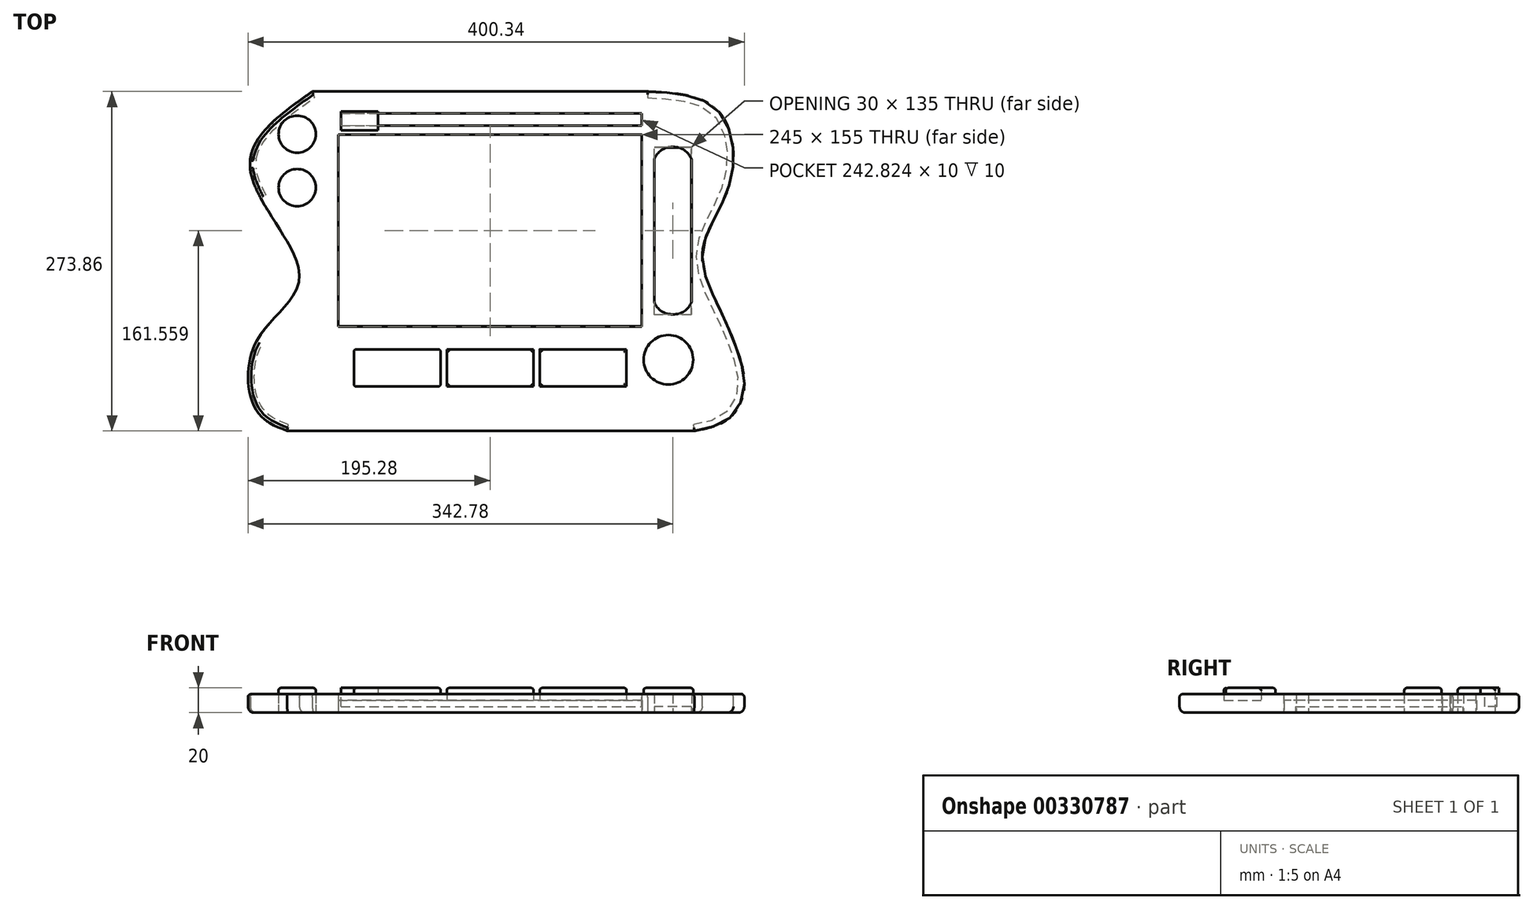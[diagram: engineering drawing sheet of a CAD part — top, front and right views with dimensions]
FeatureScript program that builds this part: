
annotation { "Feature Type Name" : "Feature", "Feature Type Description" : "" }
export const myFeature = defineFeature(function(context is Context, id is Id, definition is map)
    precondition{}
    {
        {
            var Q0;
            Q0=qCreatedBy(makeId("Top.planeOp"),FACE);
            var sketch = newSketch(context, id + "F0", { "sketchPlane" : qUnion([Q0])});
            skLineSegment(sketch, "E0.bottom", {"start": v(164.72, -136.93) * mm, "end": v(-163.68, -136.93) * mm});
            skLineSegment(sketch, "E0.top", {"start": v(127.2, 136.93) * mm, "end": v(-143.35, 136.93) * mm});
            skPoint(sketch, "E0.middle", {"position": v(0, 0) * mm});
            skFitSpline(sketch, "E1", {"points": [v(-143.35, 136.93) * mm, v(-193.66, 75.02) * mm, v(-153.78, -11.5) * mm, v(-188.18, -64.16) * mm, v(-188.7, -119.93) * mm, v(-163.68, -136.93) * mm], "startDerivative": vector(-350.4, -246.16) * mm, "endDerivative": vector(205.8, -79.15) * mm});
            skPoint(sketch, "E2.orphan", {"position": v(-193.66, 136.93) * mm});
            skLineSegment(sketch, "E3.trimOffspring", {"start": v(-193.66, 75.02) * mm, "end": v(-193.66, 81.28) * mm});
            skPoint(sketch, "E4.orphan", {"position": v(-193.66, -136.93) * mm});
            skFitSpline(sketch, "E5", {"points": [v(127.2, 136.93) * mm, v(183.49, 121.94) * mm, v(193.66, 64.08) * mm, v(171.5, 9.34) * mm, v(186.1, -40.7) * mm, v(204.86, -94.4) * mm, v(199.65, -118.9) * mm, v(186.62, -130.88) * mm, v(164.72, -136.93) * mm], "startDerivative": vector(444.92, -23.16) * mm, "endDerivative": vector(-254.64, -48.14) * mm});
            skPoint(sketch, "E6.orphan", {"position": v(193.66, 136.93) * mm});
            skPoint(sketch, "E0.left.start.orphan", {"position": v(193.66, -136.93) * mm});
            skFitSpline(sketch, "E7", {"points": [v(-193.66, 81.28) * mm, v(-184.53, 113.6) * mm, v(-160.55, 132.36) * mm, v(-143.35, 136.93) * mm], "startDerivative": vector(12.3, 93.1) * mm, "endDerivative": vector(59.92, 10.35) * mm});
            skFitSpline(sketch, "E8", {"points": [v(-184.98, 50.85) * mm, v(-169.94, 0) * mm, v(-176.2, -30.8) * mm, v(-188.18, -64.16) * mm], "startDerivative": vector(55.2, -140.26) * mm, "endDerivative": vector(-39.02, -107.81) * mm});
            skLineSegment(sketch, "E9.bottom", {"start": v(122.5, 102.13) * mm, "end": v(-122.5, 102.13) * mm});
            skLineSegment(sketch, "E9.left", {"start": v(122.5, 102.13) * mm, "end": v(122.5, -52.87) * mm});
            skLineSegment(sketch, "E9.right", {"start": v(-122.5, 102.13) * mm, "end": v(-122.5, -52.87) * mm});
            skLineSegment(sketch, "E10", {"start": v(-122.5, -52.87) * mm, "end": v(122.5, -52.87) * mm});
            skPoint(sketch, "E9.top.end.orphan", {"position": v(-122.5, -102.13) * mm});
            skPoint(sketch, "E11.orphan", {"position": v(122.5, -102.13) * mm});
            skLineSegment(sketch, "E12.bottom", {"start": v(149.2, -42.87) * mm, "end": v(145.8, -42.87) * mm});
            skLineSegment(sketch, "E12.top", {"start": v(149.2, 92.13) * mm, "end": v(145.8, 92.13) * mm});
            skLineSegment(sketch, "E12.left", {"start": v(162.5, -32.87) * mm, "end": v(162.5, 82.13) * mm});
            skLineSegment(sketch, "E12.right", {"start": v(132.5, -32.87) * mm, "end": v(132.5, 82.13) * mm});
            skPoint(sketch, "E12.middle", {"position": v(147.5, 24.63) * mm});
            skPoint(sketch, "E13.start.orphan", {"position": v(147.5, 92.13) * mm});
            skPoint(sketch, "E14.start.orphan", {"position": v(122.5, 24.63) * mm});
            skArc(sketch, "E15", {"start": v(147.5, 92.13) * mm, "mid": v(138.33, 89.63) * mm, "end": v(132.5, 82.13) * mm});
            skArc(sketch, "E16", {"start": v(162.5, 82.13) * mm, "mid": v(156.67, 89.63) * mm, "end": v(147.5, 92.13) * mm});
            skPoint(sketch, "E17.orphan", {"position": v(162.5, 92.13) * mm});
            skPoint(sketch, "E18.orphan", {"position": v(132.5, 92.13) * mm});
            skArc(sketch, "E19", {"start": v(132.5, -32.87) * mm, "mid": v(138.33, -40.38) * mm, "end": v(147.5, -42.87) * mm});
            skArc(sketch, "E20", {"start": v(147.5, -42.87) * mm, "mid": v(156.67, -40.38) * mm, "end": v(162.5, -32.87) * mm});
            skPoint(sketch, "E21.orphan", {"position": v(162.5, -42.87) * mm});
            skPoint(sketch, "E22.end.orphan", {"position": v(147.5, -32.87) * mm});
            skPoint(sketch, "E23.orphan", {"position": v(132.5, -42.87) * mm});
            skSolve(sketch);
        }
        {
            var Q0;
            Q0=qCreatedBy(makeId("Top.planeOp"),FACE);
            var sketch = newSketch(context, id + "F1", { "sketchPlane" : qUnion([Q0])});
            skLineSegment(sketch, "E24.left", {"start": v(-122.57, 77.55) * mm, "end": v(-122.57, -52.49) * mm});
            skLineSegment(sketch, "E24.right", {"start": v(122.57, 77.55) * mm, "end": v(122.57, -52.49) * mm});
            skPoint(sketch, "E24.middle", {"position": v(0, 0) * mm});
            skLineSegment(sketch, "E25", {"start": v(-122.57, -52.49) * mm, "end": v(122.57, -52.49) * mm});
            skLineSegment(sketch, "E26", {"start": v(122.57, -52.49) * mm, "end": v(122.57, 102.51) * mm});
            skLineSegment(sketch, "E27", {"start": v(122.57, 102.51) * mm, "end": v(-122.43, 102.51) * mm});
            skLineSegment(sketch, "E28", {"start": v(-122.43, 102.51) * mm, "end": v(-122.57, 77.55) * mm});
            skPoint(sketch, "E29.orphan", {"position": v(-122.57, -77.55) * mm});
            skPoint(sketch, "E30.orphan", {"position": v(122.57, -77.55) * mm});
            skSolve(sketch);
        }
        {
            var Q0;
            Q0=makeQuery(id+"F0.imprint","IMPRINT",FACE,{"disambiguationData":[TD([[makeQuery(id+"F0.imprint","IMPRINT",EDGE,{"derivedFrom":sQuery(id+"F0.wireOp",EDGE,"E9.bottom")}),1.0]])]});
            var sketch = newSketch(context, id + "F2", { "sketchPlane" : qUnion([Q0])});
            skLineSegment(sketch, "E31.bottom", {"start": v(-109.92, -71.15) * mm, "end": v(-39.92, -71.15) * mm});
            skLineSegment(sketch, "E31.top", {"start": v(-109.92, -101.15) * mm, "end": v(-39.92, -101.15) * mm});
            skLineSegment(sketch, "E31.left", {"start": v(-109.92, -71.15) * mm, "end": v(-109.92, -101.15) * mm});
            skLineSegment(sketch, "E31.right", {"start": v(110.08, -71.15) * mm, "end": v(110.08, -101.15) * mm});
            skPoint(sketch, "E32.end.orphan", {"position": v(0, -61.68) * mm});
            skLineSegment(sketch, "E33", {"start": v(40.08, -86.15) * mm, "end": v(35.08, -86.15) * mm, "construction": true});
            skLineSegment(sketch, "E34", {"start": v(-39.92, -86.15) * mm, "end": v(-39.92, -101.15) * mm});
            skLineSegment(sketch, "E35", {"start": v(-39.92, -101.15) * mm, "end": v(-39.92, -71.15) * mm});
            skPoint(sketch, "E35.endSnap0", {"position": v(-39.92, -93.65) * mm});
            skLineSegment(sketch, "E36", {"start": v(-34.92, -86.15) * mm, "end": v(-34.92, -71.15) * mm});
            skLineSegment(sketch, "E37", {"start": v(-34.92, -71.15) * mm, "end": v(-34.92, -101.15) * mm});
            skLineSegment(sketch, "E38", {"start": v(40.08, -86.15) * mm, "end": v(40.08, -71.15) * mm});
            skLineSegment(sketch, "E39", {"start": v(40.08, -71.15) * mm, "end": v(40.08, -101.15) * mm});
            skLineSegment(sketch, "E40", {"start": v(35.08, -86.15) * mm, "end": v(35.08, -71.15) * mm});
            skLineSegment(sketch, "E41", {"start": v(35.08, -71.15) * mm, "end": v(35.08, -101.15) * mm});
            skPoint(sketch, "E42.start.orphan", {"position": v(-109.92, -86.15) * mm});
            skPoint(sketch, "E43.start.orphan", {"position": v(110.08, -86.15) * mm});
            skLineSegment(sketch, "E44.trimOffspring", {"start": v(-34.92, -71.15) * mm, "end": v(35.08, -71.15) * mm});
            skLineSegment(sketch, "E45.trimOffspring", {"start": v(-34.92, -101.15) * mm, "end": v(110.08, -101.15) * mm});
            skLineSegment(sketch, "E46.trimOffspring", {"start": v(40.08, -71.15) * mm, "end": v(110.08, -71.15) * mm});
            skSolve(sketch);
        }
        {
            var Q0;
            Q0=makeQuery(id+"F0.imprint","IMPRINT",FACE,{"disambiguationData":[TD([[makeQuery(id+"F0.imprint","IMPRINT",EDGE,{"derivedFrom":sQuery(id+"F0.wireOp",EDGE,"E9.bottom")}),1.0]])]});
            var sketch = newSketch(context, id + "F3", { "sketchPlane" : qUnion([Q0])});
            skCircle(sketch, "E47", {"center": v(-155.62, 102.5) * mm, "radius": 15 * mm});
            skCircle(sketch, "E48", {"center": v(-155.62, 59.4) * mm, "radius": 15 * mm});
            skSolve(sketch);
        }
        {
            var Q0;
            Q0=makeQuery(id+"F0.imprint","IMPRINT",FACE,{"disambiguationData":[TD([[makeQuery(id+"F0.imprint","IMPRINT",EDGE,{"derivedFrom":sQuery(id+"F0.wireOp",EDGE,"E0.bottom")}),-1.0]])]});
            extrude(context, id + "F4", {"entities" : qUnion([Q0]), "depth" : 15 * mm});
        }
        {
            var Q0;
            Q0 = qSketchRegion(id + "F1", true);
            extrude(context, id + "F5", {"entities" : qUnion([Q0]), "depth" : 10 * mm});
        }
        {
            var Q0;
            Q0 = qSketchRegion(id + "F2", true);
            extrude(context, id + "F6", {"entities" : qUnion([Q0]), "depth" : 20 * mm, "hasSecondDirection" : true, "secondDirectionOppositeDirection" : false, "secondDirectionDepth" : 10 * mm});
        }
        {
            var Q0;
            {var subQ9=sQuery(id+"F0.wireOp",EDGE,"E12.left");Q0=makeQuery(id+"F0.imprint","IMPRINT",FACE,{"disambiguationData":[TD([[makeQuery(id+"F0.imprint","IMPRINT",EDGE,{"derivedFrom":subQ9}),1.0]])]});}
            var sketch = newSketch(context, id + "F7", { "sketchPlane" : qUnion([Q0])});
            skLineSegment(sketch, "E49.bottom", {"start": v(162.38, -43.34) * mm, "end": v(132.38, -43.34) * mm});
            skLineSegment(sketch, "E49.top", {"start": v(162.38, 91.66) * mm, "end": v(132.38, 91.66) * mm});
            skLineSegment(sketch, "E49.left", {"start": v(162.38, -43.34) * mm, "end": v(162.38, 91.66) * mm});
            skLineSegment(sketch, "E49.right", {"start": v(132.38, -43.34) * mm, "end": v(132.38, 91.66) * mm});
            skPoint(sketch, "E49.middle", {"position": v(147.38, 24.16) * mm});
            skSolve(sketch);
        }
        {
            var Q0;
            Q0 = qSketchRegion(id + "F7", true);
            extrude(context, id + "F8", {"entities" : qUnion([Q0]), "depth" : 5 * mm});
        }
        {
            var Q0;
            Q0=qCreatedBy(makeId("Top.planeOp"),FACE);
            var sketch = newSketch(context, id + "F9", { "sketchPlane" : qUnion([Q0])});
            skCircle(sketch, "E50", {"center": v(143.85, -79.57) * mm, "radius": 20 * mm});
            skSolve(sketch);
        }
        {
            var Q0;
            Q0 = qSketchRegion(id + "F3", true);
            extrude(context, id + "F10", {"entities" : qUnion([Q0]), "depth" : 20 * mm});
        }
        {
            var Q0;
            Q0 = qSketchRegion(id + "F9", true);
            extrude(context, id + "F11", {"entities" : qUnion([Q0]), "operationType" : NewBodyOperationType.ADD, "depth" : 20 * mm});
        }
        {
            var Q0;
            Q0=makeQuery(id+"F4.opExtrude","CAP_EDGE",EDGE,{"disambiguationData":[OSD([sQuery(id+"F0.wireOp",EDGE,"E0.bottom")])],"isStart":false});
            var Q1;
            Q1=makeQuery(id+"F4.opExtrude","CAP_EDGE",EDGE,{"disambiguationData":[OSD([sQuery(id+"F0.wireOp",EDGE,"E1")])],"isStart":false});
            var Q2;
            Q2=makeQuery(id+"F4.opExtrude","CAP_EDGE",EDGE,{"disambiguationData":[OSD([sQuery(id+"F0.wireOp",EDGE,"E8")])],"isStart":false});
            var Q3;
            Q3=makeQuery(id+"F4.opExtrude","CAP_EDGE",EDGE,{"disambiguationData":[OSD([sQuery(id+"F0.wireOp",EDGE,"E1")])],"isStart":false});
            var Q4;
            Q4=makeQuery(id+"F4.opExtrude","CAP_EDGE",EDGE,{"disambiguationData":[OSD([sQuery(id+"F0.wireOp",EDGE,"E3.trimOffspring")])],"isStart":false});
            var Q5;
            Q5=makeQuery(id+"F4.opExtrude","CAP_EDGE",EDGE,{"disambiguationData":[OSD([sQuery(id+"F0.wireOp",EDGE,"E7")])],"isStart":false});
            var Q6;
            Q6=makeQuery(id+"F4.opExtrude","CAP_EDGE",EDGE,{"disambiguationData":[OSD([sQuery(id+"F0.wireOp",EDGE,"E0.top")])],"isStart":false});
            var Q7;
            Q7=makeQuery(id+"F4.opExtrude","CAP_EDGE",EDGE,{"disambiguationData":[OSD([sQuery(id+"F0.wireOp",EDGE,"E5")])],"isStart":false});
            fillet(context, id + "F12", {"entities" : qUnion([Q0, Q1, Q2, Q3, Q4, Q5, Q6, Q7]), "radius" : 2.5 * mm, "tangentPropagation" : true, "allowEdgeOverflow" : false});
        }
        {
            var Q0;
            Q0=makeQuery(id+"F6.opExtrude","CAP_EDGE",EDGE,{"disambiguationData":[OSD([sQuery(id+"F2.wireOp",EDGE,"E31.top")])],"isStart":false});
            var Q1;
            Q1=makeQuery(id+"F6.opExtrude","CAP_EDGE",EDGE,{"disambiguationData":[OSD([sQuery(id+"F2.wireOp",EDGE,"E35")])],"isStart":false});
            var Q2;
            Q2=makeQuery(id+"F6.opExtrude","CAP_EDGE",EDGE,{"disambiguationData":[OSD([sQuery(id+"F2.wireOp",EDGE,"E31.bottom")])],"isStart":false});
            var Q3;
            Q3=makeQuery(id+"F6.opExtrude","CAP_EDGE",EDGE,{"disambiguationData":[OSD([sQuery(id+"F2.wireOp",EDGE,"E31.left")])],"isStart":false});
            var Q4;
            {var subQ0=sQuery(id+"F2.wireOp",EDGE,"E45.trimOffspring");Q4=makeQuery(id+"F6.opExtrude","CAP_EDGE",EDGE,{"disambiguationData":[OSD([subQ0]),TDD([makeQuery(id+"F2.imprint","IMPRINT",EDGE,{"disambiguationData":[TD([[makeQuery(id+"F2.imprint","INTERSECT",VERTEX,{"derivedFrom":[sQuery(id+"F2.wireOp",EDGE,"E37"),subQ0]}),-1.0]])],"derivedFrom":subQ0})])],"isStart":false});}
            var Q5;
            Q5=makeQuery(id+"F6.opExtrude","CAP_EDGE",EDGE,{"disambiguationData":[OSD([sQuery(id+"F2.wireOp",EDGE,"E41")])],"isStart":false});
            var Q6;
            Q6=makeQuery(id+"F6.opExtrude","CAP_EDGE",EDGE,{"disambiguationData":[OSD([sQuery(id+"F2.wireOp",EDGE,"E44.trimOffspring")])],"isStart":false});
            var Q7;
            Q7=makeQuery(id+"F6.opExtrude","CAP_EDGE",EDGE,{"disambiguationData":[OSD([sQuery(id+"F2.wireOp",EDGE,"E37")])],"isStart":false});
            var Q8;
            {var subQ0=sQuery(id+"F2.wireOp",EDGE,"E45.trimOffspring");Q8=makeQuery(id+"F6.opExtrude","CAP_EDGE",EDGE,{"disambiguationData":[OSD([subQ0]),TDD([makeQuery(id+"F2.imprint","IMPRINT",EDGE,{"disambiguationData":[TD([[makeQuery(id+"F2.imprint","INTERSECT",VERTEX,{"derivedFrom":[sQuery(id+"F2.wireOp",EDGE,"E31.right"),subQ0]}),1.0]])],"derivedFrom":subQ0})])],"isStart":false});}
            var Q9;
            Q9=makeQuery(id+"F6.opExtrude","CAP_EDGE",EDGE,{"disambiguationData":[OSD([sQuery(id+"F2.wireOp",EDGE,"E31.right")])],"isStart":false});
            var Q10;
            Q10=makeQuery(id+"F6.opExtrude","CAP_EDGE",EDGE,{"disambiguationData":[OSD([sQuery(id+"F2.wireOp",EDGE,"E46.trimOffspring")])],"isStart":false});
            var Q11;
            Q11=makeQuery(id+"F6.opExtrude","CAP_EDGE",EDGE,{"disambiguationData":[OSD([sQuery(id+"F2.wireOp",EDGE,"E39")])],"isStart":false});
            var Q12;
            Q12=makeQuery(id+"F6.opExtrude","SWEPT_EDGE",EDGE,{"disambiguationData":[OSD([sQuery(id+"F2.wireOp",EDGE,"E31.bottom"),sQuery(id+"F2.wireOp",EDGE,"E31.left")])]});
            var Q13;
            Q13=makeQuery(id+"F6.opExtrude","SWEPT_EDGE",EDGE,{"disambiguationData":[OSD([sQuery(id+"F2.wireOp",EDGE,"E31.bottom"),sQuery(id+"F2.wireOp",EDGE,"E35")])]});
            var Q14;
            Q14=makeQuery(id+"F6.opExtrude","SWEPT_EDGE",EDGE,{"disambiguationData":[OSD([sQuery(id+"F2.wireOp",EDGE,"E31.top"),sQuery(id+"F2.wireOp",EDGE,"E35")])]});
            var Q15;
            Q15=makeQuery(id+"F6.opExtrude","SWEPT_EDGE",EDGE,{"disambiguationData":[OSD([sQuery(id+"F2.wireOp",EDGE,"E31.top"),sQuery(id+"F2.wireOp",EDGE,"E31.left")])]});
            fillet(context, id + "F13", {"entities" : qUnion([Q0, Q1, Q2, Q3, Q4, Q5, Q6, Q7, Q8, Q9, Q10, Q11, Q12, Q13, Q14, Q15]), "radius" : 2 * mm, "tangentPropagation" : true, "allowEdgeOverflow" : false});
        }
        {
            var Q0;
            Q0=makeQuery(id+"F10.opExtrude","CAP_EDGE",EDGE,{"disambiguationData":[OSD([sQuery(id+"F3.wireOp",EDGE,"E48")])],"isStart":false});
            var Q1;
            Q1=makeQuery(id+"F10.opExtrude","CAP_EDGE",EDGE,{"disambiguationData":[OSD([sQuery(id+"F3.wireOp",EDGE,"E47")])],"isStart":false});
            fillet(context, id + "F14", {"entities" : qUnion([Q0, Q1]), "radius" : 2 * mm, "tangentPropagation" : true, "allowEdgeOverflow" : false});
        }
        {
            var Q0;
            Q0=makeQuery(id+"F4.opExtrude","CAP_EDGE",EDGE,{"disambiguationData":[OSD([sQuery(id+"F0.wireOp",EDGE,"E7")])],"isStart":true});
            var Q1;
            Q1=makeQuery(id+"F4.opExtrude","CAP_EDGE",EDGE,{"disambiguationData":[OSD([sQuery(id+"F0.wireOp",EDGE,"E1")])],"isStart":true});
            var Q2;
            Q2=makeQuery(id+"F4.opExtrude","CAP_EDGE",EDGE,{"disambiguationData":[OSD([sQuery(id+"F0.wireOp",EDGE,"E3.trimOffspring")])],"isStart":true});
            var Q3;
            Q3=makeQuery(id+"F4.opExtrude","CAP_EDGE",EDGE,{"disambiguationData":[OSD([sQuery(id+"F0.wireOp",EDGE,"E8")])],"isStart":true});
            var Q4;
            Q4=makeQuery(id+"F4.opExtrude","CAP_EDGE",EDGE,{"disambiguationData":[OSD([sQuery(id+"F0.wireOp",EDGE,"E1")])],"isStart":true});
            var Q5;
            Q5=makeQuery(id+"F4.opExtrude","CAP_EDGE",EDGE,{"disambiguationData":[OSD([sQuery(id+"F0.wireOp",EDGE,"E0.bottom")])],"isStart":true});
            var Q6;
            Q6=makeQuery(id+"F4.opExtrude","CAP_EDGE",EDGE,{"disambiguationData":[OSD([sQuery(id+"F0.wireOp",EDGE,"E0.top")])],"isStart":true});
            var Q7;
            Q7=makeQuery(id+"F4.opExtrude","CAP_EDGE",EDGE,{"disambiguationData":[OSD([sQuery(id+"F0.wireOp",EDGE,"E5")])],"isStart":true});
            fillet(context, id + "F15", {"entities" : qUnion([Q0, Q1, Q2, Q3, Q4, Q5, Q6, Q7]), "radius" : 5 * mm, "tangentPropagation" : true, "allowEdgeOverflow" : false});
        }
        {
            var Q0;
            Q0=makeQuery(id+"F11.opExtrude","CAP_EDGE",EDGE,{"disambiguationData":[OSD([sQuery(id+"F9.wireOp",EDGE,"E50")])],"isStart":false});
            fillet(context, id + "F16", {"entities" : qUnion([Q0]), "radius" : 2 * mm, "tangentPropagation" : true, "allowEdgeOverflow" : false});
        }
        {
            var Q0;
            Q0=makeQuery(id+"F4.opExtrude","CAP_FACE",FACE,{"disambiguationData":[OSD([sQuery(id+"F0.wireOp",EDGE,"E0.bottom"),sQuery(id+"F0.wireOp",EDGE,"E0.top"),sQuery(id+"F0.wireOp",EDGE,"E1"),sQuery(id+"F0.wireOp",EDGE,"E3.trimOffspring"),sQuery(id+"F0.wireOp",EDGE,"E5"),sQuery(id+"F0.wireOp",EDGE,"E7"),sQuery(id+"F0.wireOp",EDGE,"E8"),sQuery(id+"F0.wireOp",EDGE,"E1"),sQuery(id+"F0.wireOp",EDGE,"E9.bottom"),sQuery(id+"F0.wireOp",EDGE,"E9.left"),sQuery(id+"F0.wireOp",EDGE,"E9.right"),sQuery(id+"F0.wireOp",EDGE,"E10"),sQuery(id+"F0.wireOp",EDGE,"E12.left"),sQuery(id+"F0.wireOp",EDGE,"E12.right"),sQuery(id+"F0.wireOp",EDGE,"E15"),sQuery(id+"F0.wireOp",EDGE,"E16"),sQuery(id+"F0.wireOp",EDGE,"E19"),sQuery(id+"F0.wireOp",EDGE,"E20")])],"isStart":false});
            var sketch = newSketch(context, id + "F17", { "sketchPlane" : qUnion([Q0])});
            skLineSegment(sketch, "E51.bottom", {"start": v(-120.32, 119.32) * mm, "end": v(122.5, 119.32) * mm});
            skLineSegment(sketch, "E51.top", {"start": v(-120.32, 109.32) * mm, "end": v(122.5, 109.32) * mm});
            skLineSegment(sketch, "E51.left", {"start": v(-120.32, 119.32) * mm, "end": v(-120.32, 109.32) * mm});
            skLineSegment(sketch, "E51.right", {"start": v(122.5, 119.32) * mm, "end": v(122.5, 109.32) * mm});
            skPoint(sketch, "E52.orphan", {"position": v(122.5, 126.13) * mm});
            skSolve(sketch);
        }
        {
            var Q0;
            Q0 = qSketchRegion(id + "F17", true);
            extrude(context, id + "F18", {"entities" : qUnion([Q0]), "operationType" : NewBodyOperationType.REMOVE, "oppositeDirection" : true, "depth" : 10 * mm});
        }
        {
            var Q0;
            Q0=makeQuery(id+"F17.imprint","IMPRINT",FACE,{"disambiguationData":[TD([[makeQuery(id+"F17.imprint","IMPRINT",EDGE,{"derivedFrom":sQuery(id+"F17.wireOp",EDGE,"E51.bottom")}),1.0]])]});
            var sketch = newSketch(context, id + "F19", { "sketchPlane" : qUnion([Q0])});
            skLineSegment(sketch, "E53", {"start": v(-120.3, 113.21) * mm, "end": v(-90.3, 113.21) * mm, "construction": true});
            skLineSegment(sketch, "E54.bottom", {"start": v(-90.3, 120.71) * mm, "end": v(-120.3, 120.71) * mm});
            skLineSegment(sketch, "E54.top", {"start": v(-90.3, 105.71) * mm, "end": v(-120.3, 105.71) * mm});
            skLineSegment(sketch, "E54.left", {"start": v(-90.3, 120.71) * mm, "end": v(-90.3, 105.71) * mm});
            skLineSegment(sketch, "E54.right", {"start": v(-120.3, 120.71) * mm, "end": v(-120.3, 105.71) * mm});
            skPoint(sketch, "E54.middle", {"position": v(-105.3, 113.21) * mm});
            skSolve(sketch);
        }
        {
            var Q0;
            Q0 = qSketchRegion(id + "F19", true);
            extrude(context, id + "F20", {"entities" : qUnion([Q0]), "operationType" : NewBodyOperationType.ADD, "depth" : 5 * mm});
        }
        {
            var Q0;
            Q0=makeQuery(id+"F6.opExtrude","CAP_FACE",FACE,{"disambiguationData":[OSD([sQuery(id+"F2.wireOp",EDGE,"E31.bottom"),sQuery(id+"F2.wireOp",EDGE,"E31.top"),sQuery(id+"F2.wireOp",EDGE,"E31.left"),sQuery(id+"F2.wireOp",EDGE,"E35")])],"isStart":true});
            var sketch = newSketch(context, id + "F21", { "sketchPlane" : qUnion([Q0])});
            skLineSegment(sketch, "E55.0", {"start": v(-111.92, 103.15) * mm, "end": v(-111.92, 69.15) * mm});
            skLineSegment(sketch, "E55.1", {"start": v(-37.92, 103.15) * mm, "end": v(-111.92, 103.15) * mm});
            skLineSegment(sketch, "E55.2", {"start": v(-37.92, 69.15) * mm, "end": v(-37.92, 103.15) * mm});
            skLineSegment(sketch, "E55.3", {"start": v(-111.92, 69.15) * mm, "end": v(-37.92, 69.15) * mm});
            skSolve(sketch);
        }
        {
            var Q0;
            Q0 = qSketchRegion(id + "F21", true);
            extrude(context, id + "F22", {"entities" : qUnion([Q0]), "operationType" : NewBodyOperationType.ADD, "oppositeDirection" : true, "depth" : 2 * mm});
        }
    });
